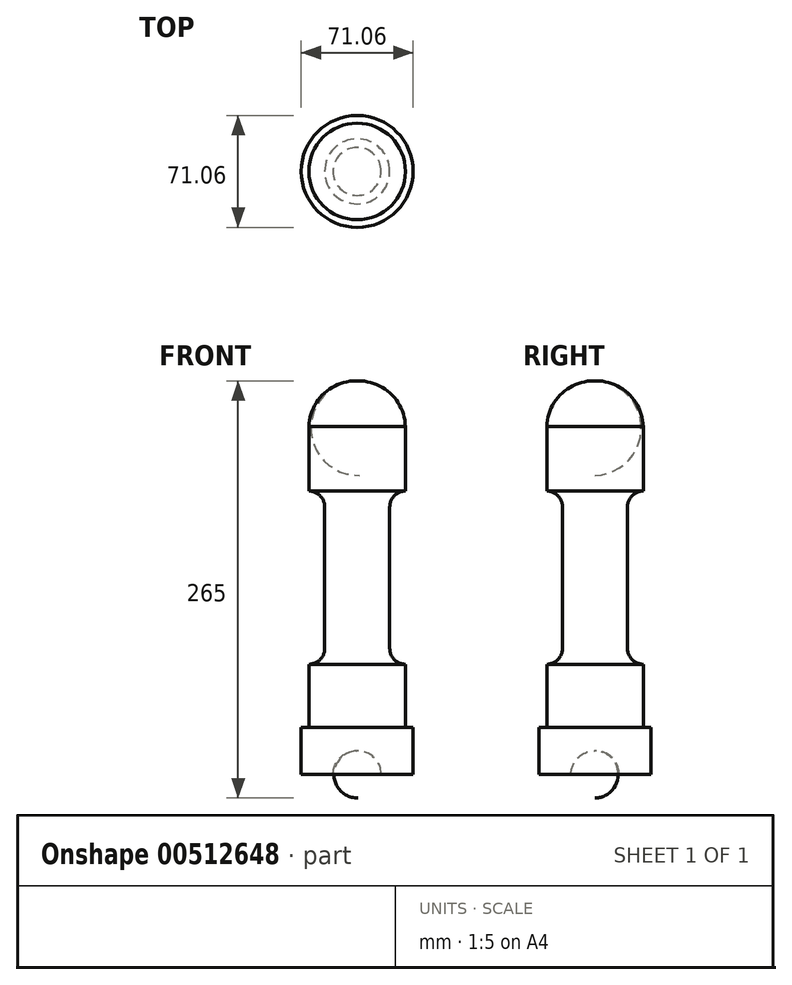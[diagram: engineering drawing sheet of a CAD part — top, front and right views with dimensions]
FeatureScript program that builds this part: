
annotation { "Feature Type Name" : "Feature", "Feature Type Description" : "" }
export const myFeature = defineFeature(function(context is Context, id is Id, definition is map)
    precondition{}
    {
        {
            var Q0;
            Q0=qCreatedBy(makeId("Front.planeOp"),FACE);
            var sketch = newSketch(context, id + "F0", { "sketchPlane" : qUnion([Q0])});
            skLineSegment(sketch, "E0.top", {"start": v(35, -124.45) * mm, "end": v(14.73, -124.45) * mm});
            skPoint(sketch, "E0.middle", {"position": v(0, 0) * mm});
            skLineSegment(sketch, "E1.bottom", {"start": v(-35.53, -124.45) * mm, "end": v(-15.27, -124.45) * mm});
            skLineSegment(sketch, "E1.top", {"start": v(-35.53, -94.45) * mm, "end": v(-30.66, -94.45) * mm});
            skLineSegment(sketch, "E1.left", {"start": v(-35.53, -124.45) * mm, "end": v(-35.53, -94.45) * mm});
            skLineSegment(sketch, "E1.right", {"start": v(34.2, -124.45) * mm, "end": v(34.2, -94.45) * mm});
            skArc(sketch, "E2", {"start": v(14.73, -124.45) * mm, "mid": v(-0.27, -109.45) * mm, "end": v(-15.27, -124.45) * mm});
            skLineSegment(sketch, "E3.trimOffspring", {"start": v(14.73, -124.45) * mm, "end": v(34.2, -124.45) * mm});
            skLineSegment(sketch, "E4.trimOffspring", {"start": v(-15.27, -124.45) * mm, "end": v(-35.53, -124.45) * mm});
            skPoint(sketch, "E5.middle", {"position": v(-0.66, -94.45) * mm});
            skPoint(sketch, "E5.top.start.orphan", {"position": v(-20.88, -131.45) * mm});
            skPoint(sketch, "E6.orphan", {"position": v(19.12, -134.45) * mm});
            skLineSegment(sketch, "E7.trimOffspring", {"start": v(29.34, -94.45) * mm, "end": v(34.2, -94.45) * mm});
            skLineSegment(sketch, "E8.trimOffspring", {"start": v(-35.53, -94.45) * mm, "end": v(-35.53, -124.45) * mm});
            skLineSegment(sketch, "E9.trimOffspring", {"start": v(34.2, -94.45) * mm, "end": v(35, -124.45) * mm});
            skLineSegment(sketch, "E10.top", {"start": v(-30.66, -54.45) * mm, "end": v(-30.66, -54.45) * mm});
            skLineSegment(sketch, "E10.left", {"start": v(-30.66, -94.45) * mm, "end": v(-30.66, -54.45) * mm});
            skLineSegment(sketch, "E10.right", {"start": v(29.34, -94.45) * mm, "end": v(29.34, -54.45) * mm});
            skLineSegment(sketch, "E11.left", {"start": v(-20.66, 45.54) * mm, "end": v(-20.66, -44.45) * mm});
            skLineSegment(sketch, "E11.right", {"start": v(19.34, 45.55) * mm, "end": v(19.34, -44.45) * mm});
            skPoint(sketch, "E11.middle", {"position": v(-0.66, -54.45) * mm});
            skPoint(sketch, "E12.orphan", {"position": v(-20.66, -164.45) * mm});
            skPoint(sketch, "E13.orphan", {"position": v(19.34, -164.45) * mm});
            skPoint(sketch, "E14.newPointA", {"position": v(29.34, -54.45) * mm});
            skArc(sketch, "E14.filletArc", {"start": v(-30.66, -54.45) * mm, "mid": v(-23.6, -51.52) * mm, "end": v(-20.66, -44.45) * mm});
            skLineSegment(sketch, "E15", {"start": v(29.34, -54.45) * mm, "end": v(29.34, -54.45) * mm});
            skPoint(sketch, "E16.visualSharp", {"position": v(19.34, -54.45) * mm});
            skArc(sketch, "E16.filletArc", {"start": v(19.34, -44.45) * mm, "mid": v(22.26, -51.52) * mm, "end": v(29.34, -54.45) * mm});
            skLineSegment(sketch, "E17.left", {"start": v(29.34, 96.27) * mm, "end": v(29.34, 55.55) * mm});
            skLineSegment(sketch, "E17.right", {"start": v(-30.66, 96.56) * mm, "end": v(-30.66, 55.54) * mm});
            skPoint(sketch, "E17.middle", {"position": v(-0.66, 55.55) * mm});
            skLineSegment(sketch, "E18", {"start": v(-30.66, 55.54) * mm, "end": v(-30.67, 55.54) * mm});
            skLineSegment(sketch, "E19", {"start": v(29.33, 55.55) * mm, "end": v(29.34, 55.55) * mm});
            skPoint(sketch, "E20.orphan", {"position": v(29.34, -14.45) * mm});
            skPoint(sketch, "E21.orphan", {"position": v(-30.66, -14.46) * mm});
            skPoint(sketch, "E22.endSnap0", {"position": v(-0.66, 125.55) * mm});
            skArc(sketch, "E23", {"start": v(29.34, 94.83) * mm, "mid": v(0.2, 125.54) * mm, "end": v(-30.66, 96.56) * mm});
            skPoint(sketch, "E22.start.orphan", {"position": v(-0.66, 125.55) * mm});
            skLineSegment(sketch, "E24", {"start": v(-30.66, 96.56) * mm, "end": v(-30.66, 96.56) * mm});
            skPoint(sketch, "E17.bottom.end.orphan", {"position": v(-30.66, 125.54) * mm});
            skPoint(sketch, "E25.orphan", {"position": v(29.34, 125.55) * mm});
            skPoint(sketch, "E26.visualSharp", {"position": v(-20.66, 55.55) * mm});
            skArc(sketch, "E26.filletArc", {"start": v(-20.66, 45.54) * mm, "mid": v(-23.6, 52.61) * mm, "end": v(-30.67, 55.54) * mm});
            skPoint(sketch, "E27.visualSharp", {"position": v(19.34, 55.55) * mm});
            skArc(sketch, "E27.filletArc", {"start": v(29.33, 55.55) * mm, "mid": v(22.26, 52.62) * mm, "end": v(19.34, 45.55) * mm});
            skLineSegment(sketch, "E28", {"start": v(0, 161.3) * mm, "end": v(0, -153.08) * mm});
            skSolve(sketch);
        }
        {
            var Q0;
            Q0=makeQuery(id+"F0.imprint","IMPRINT",FACE,{"disambiguationData":[TD([[makeQuery(id+"F0.imprint","IMPRINT",EDGE,{"derivedFrom":sQuery(id+"F0.wireOp",EDGE,"E1.top")}),-1.0]])]});
            var Q1;
            Q1=sQuery(id+"F0.wireOp",EDGE,"E28");
            revolve(context, id + "F1", {"entities" : qUnion([Q0]), "axis" : qUnion([Q1]), "revolveType" : RevolveType.FULL});
        }
    });
